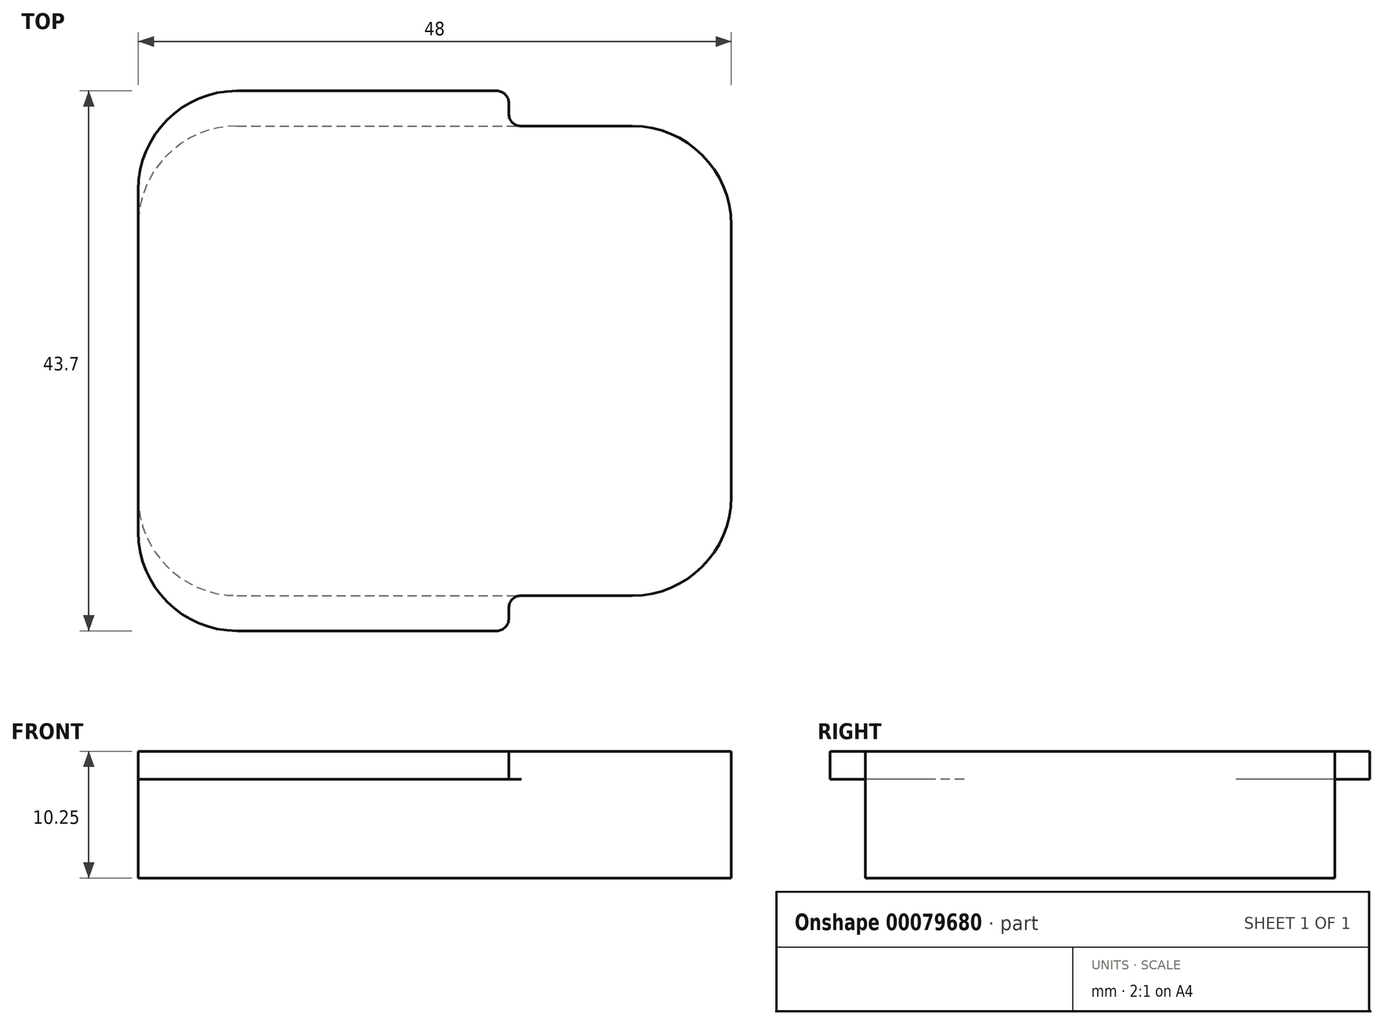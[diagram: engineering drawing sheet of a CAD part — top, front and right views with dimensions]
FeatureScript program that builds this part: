
annotation { "Feature Type Name" : "Feature", "Feature Type Description" : "" }
export const myFeature = defineFeature(function(context is Context, id is Id, definition is map)
    precondition{}
    {
        {
            var Q0;
            Q0=qCreatedBy(makeId("Top.planeOp"),FACE);
            var sketch = newSketch(context, id + "F0", { "sketchPlane" : qUnion([Q0])});
            skLineSegment(sketch, "E0.bottom", {"start": v(-16, 19) * mm, "end": v(16, 19) * mm});
            skLineSegment(sketch, "E0.top", {"start": v(-16, -19) * mm, "end": v(16, -19) * mm});
            skLineSegment(sketch, "E0.left", {"start": v(-24, 11) * mm, "end": v(-24, -11) * mm});
            skLineSegment(sketch, "E0.right", {"start": v(24, 11) * mm, "end": v(24, -11) * mm});
            skPoint(sketch, "E1.visualSharp", {"position": v(-24, 19) * mm});
            skArc(sketch, "E1.filletArc", {"start": v(-16, 19) * mm, "mid": v(-21.66, 16.66) * mm, "end": v(-24, 11) * mm});
            skPoint(sketch, "E2.visualSharp", {"position": v(24, 19) * mm});
            skArc(sketch, "E2.filletArc", {"start": v(24, 11) * mm, "mid": v(21.66, 16.66) * mm, "end": v(16, 19) * mm});
            skPoint(sketch, "E3.visualSharp", {"position": v(24, -19) * mm});
            skArc(sketch, "E3.filletArc", {"start": v(16, -19) * mm, "mid": v(21.66, -16.66) * mm, "end": v(24, -11) * mm});
            skPoint(sketch, "E4.visualSharp", {"position": v(-24, -19) * mm});
            skArc(sketch, "E4.filletArc", {"start": v(-24, -11) * mm, "mid": v(-21.66, -16.66) * mm, "end": v(-16, -19) * mm});
            skSolve(sketch);
        }
        {
            var Q0;
            Q0=makeQuery(id+"F0.imprint","IMPRINT",FACE,{"disambiguationData":[TD([[makeQuery(id+"F0.imprint","IMPRINT",EDGE,{"derivedFrom":sQuery(id+"F0.wireOp",EDGE,"E0.bottom")}),-1.0]])]});
            extrude(context, id + "F1", {"entities" : qUnion([Q0]), "depth" : 10.25 * mm});
        }
        {
            var Q0;
            Q0=makeQuery(id+"F1.opExtrude","CAP_FACE",FACE,{"disambiguationData":[OSD([sQuery(id+"F0.wireOp",EDGE,"E0.bottom"),sQuery(id+"F0.wireOp",EDGE,"E0.top"),sQuery(id+"F0.wireOp",EDGE,"E0.left"),sQuery(id+"F0.wireOp",EDGE,"E0.right"),sQuery(id+"F0.wireOp",EDGE,"E1.filletArc"),sQuery(id+"F0.wireOp",EDGE,"E2.filletArc"),sQuery(id+"F0.wireOp",EDGE,"E3.filletArc"),sQuery(id+"F0.wireOp",EDGE,"E4.filletArc")])],"isStart":false});
            var sketch = newSketch(context, id + "F2", { "sketchPlane" : qUnion([Q0])});
            skLineSegment(sketch, "E5.bottom", {"start": v(-16, 21.85) * mm, "end": v(5, 21.85) * mm});
            skLineSegment(sketch, "E5.top", {"start": v(-16, -21.85) * mm, "end": v(5, -21.85) * mm});
            skLineSegment(sketch, "E5.left", {"start": v(-24, 13.85) * mm, "end": v(-24, -13.85) * mm});
            skLineSegment(sketch, "E6", {"start": v(6, 20.85) * mm, "end": v(6, 20) * mm});
            skPoint(sketch, "E7.orphan", {"position": v(-5.53, -21.85) * mm});
            skLineSegment(sketch, "E8.bottom", {"start": v(7, 19) * mm, "end": v(8.85, 19) * mm});
            skLineSegment(sketch, "E8.top", {"start": v(7, -19) * mm, "end": v(8.85, -19) * mm});
            skLineSegment(sketch, "E8.right", {"start": v(8.85, 19) * mm, "end": v(8.85, -19) * mm});
            skLineSegment(sketch, "E9.trimOffspring", {"start": v(6, -20) * mm, "end": v(6, -20.85) * mm});
            skPoint(sketch, "E10.visualSharp", {"position": v(-24, -21.85) * mm});
            skArc(sketch, "E10.filletArc", {"start": v(-24, -13.85) * mm, "mid": v(-21.66, -19.5) * mm, "end": v(-16, -21.85) * mm});
            skPoint(sketch, "E11.visualSharp", {"position": v(-24, 21.85) * mm});
            skArc(sketch, "E11.filletArc", {"start": v(-16, 21.85) * mm, "mid": v(-21.66, 19.5) * mm, "end": v(-24, 13.85) * mm});
            skPoint(sketch, "E12.visualSharp", {"position": v(6, 21.85) * mm});
            skArc(sketch, "E12.filletArc", {"start": v(6, 20.85) * mm, "mid": v(5.7, 21.56) * mm, "end": v(5, 21.85) * mm});
            skPoint(sketch, "E13.visualSharp", {"position": v(6, 19) * mm});
            skArc(sketch, "E13.filletArc", {"start": v(6, 20) * mm, "mid": v(6.3, 19.3) * mm, "end": v(7, 19) * mm});
            skPoint(sketch, "E14.visualSharp", {"position": v(6, -21.85) * mm});
            skArc(sketch, "E14.filletArc", {"start": v(5, -21.85) * mm, "mid": v(5.7, -21.56) * mm, "end": v(6, -20.85) * mm});
            skPoint(sketch, "E15.visualSharp", {"position": v(6, -19) * mm});
            skArc(sketch, "E15.filletArc", {"start": v(7, -19) * mm, "mid": v(6.3, -19.3) * mm, "end": v(6, -20) * mm});
            skSolve(sketch);
        }
        {
            var Q0;
            Q0=makeQuery(id+"F2.imprint","IMPRINT",FACE,{"disambiguationData":[TD([[makeQuery(id+"F2.imprint","IMPRINT",EDGE,{"derivedFrom":sQuery(id+"F2.wireOp",EDGE,"E5.bottom")}),-1.0]])]});
            var Q1;
            Q1=makeQuery(id+"F2.imprint","IMPRINT",FACE,{"disambiguationData":[TD([[makeQuery(id+"F2.imprint","IMPRINT",EDGE,{"derivedFrom":sQuery(id+"F2.wireOp",EDGE,"E5.top")}),1.0]])]});
            extrude(context, id + "F3", {"entities" : qUnion([Q0, Q1]), "operationType" : NewBodyOperationType.ADD, "oppositeDirection" : true, "depth" : 2.25 * mm});
        }
    });
